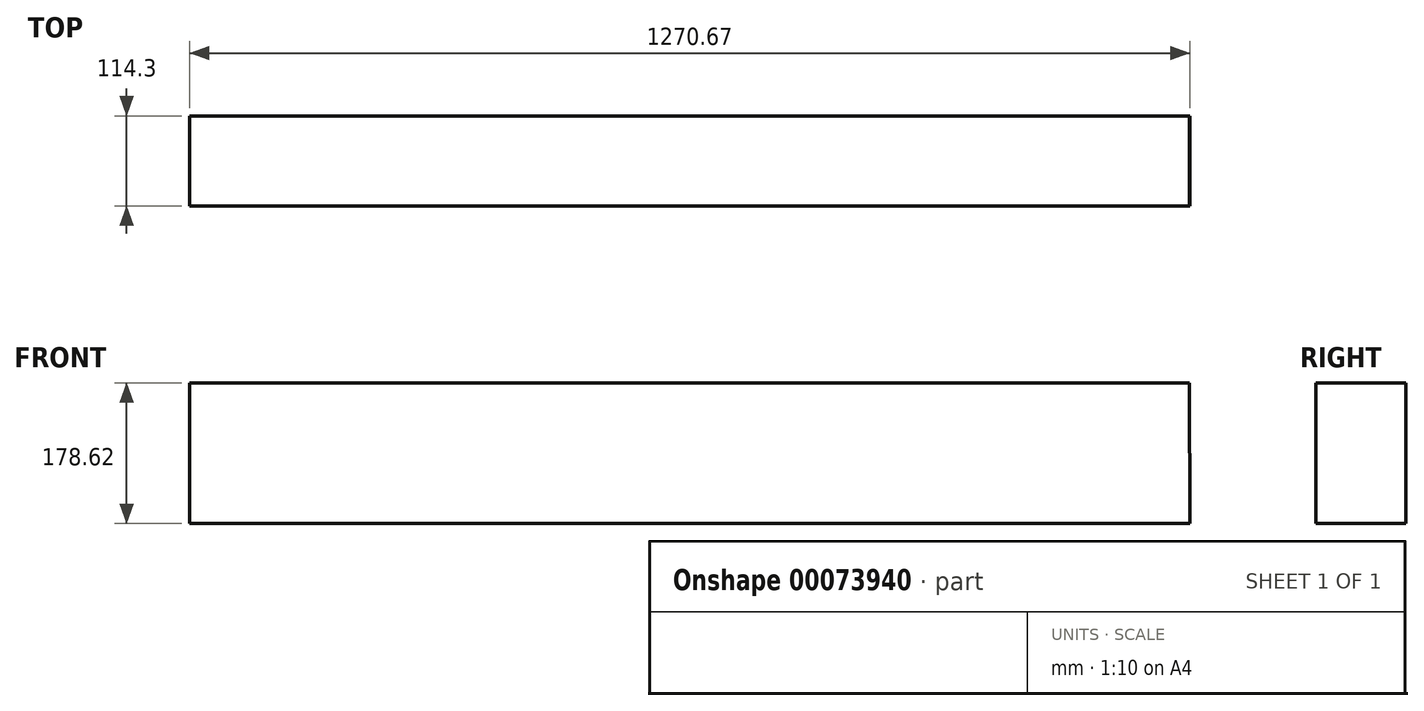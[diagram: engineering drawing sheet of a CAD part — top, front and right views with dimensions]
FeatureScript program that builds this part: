
annotation { "Feature Type Name" : "Feature", "Feature Type Description" : "" }
export const myFeature = defineFeature(function(context is Context, id is Id, definition is map)
    precondition{}
    {
        {
            var Q0;
            Q0=qCreatedBy(makeId("Front.planeOp"),FACE);
            var sketch = newSketch(context, id + "F0", { "sketchPlane" : qUnion([Q0])});
            skLineSegment(sketch, "E0", {"start": v(-433.3, 110.14) * mm, "end": v(230.04, 110.14) * mm});
            skLineSegment(sketch, "E1", {"start": v(230.04, 110.14) * mm, "end": v(632.44, 110.14) * mm});
            skLineSegment(sketch, "E2", {"start": v(632.44, 110.14) * mm, "end": v(-637.56, 110.14) * mm});
            skLineSegment(sketch, "E3", {"start": v(-637.56, 110.14) * mm, "end": v(-637.56, -68.48) * mm});
            skLineSegment(sketch, "E4", {"start": v(-637.56, -68.48) * mm, "end": v(633.11, -68.48) * mm});
            skLineSegment(sketch, "E5", {"start": v(633.11, -68.48) * mm, "end": v(632.44, 110.14) * mm});
            skSolve(sketch);
        }
        {
            var Q0;
            {var subQ2=sQuery(id+"F0.wireOp",EDGE,"E3");Q0=makeQuery(id+"F0.imprint","IMPRINT",FACE,{"disambiguationData":[TD([[makeQuery(id+"F0.imprint","IMPRINT",EDGE,{"derivedFrom":subQ2}),1.0]])]});}
            extrude(context, id + "F1", {"entities" : qUnion([Q0]), "depth" : 114.3 * mm});
        }
    });
